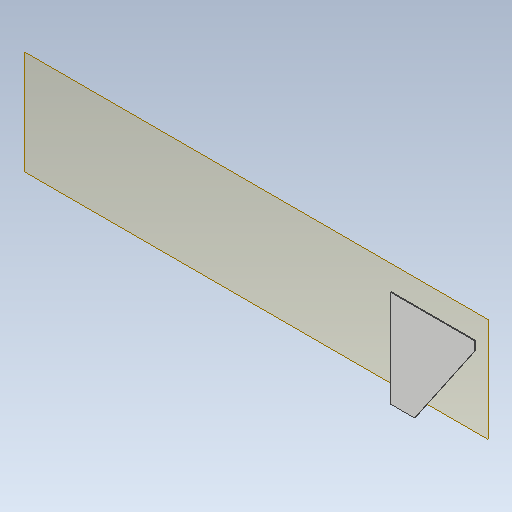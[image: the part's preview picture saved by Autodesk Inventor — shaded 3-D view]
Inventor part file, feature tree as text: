
AUTODESK INVENTOR PART (.ipt)
format: ipt  version: 2020.1 (Build 241239000, 239)  size: 121,344 bytes
history: native  units: mm
features: other x5, plane x1, sheet_metal_op x1, sketch x1
ambient origin geometry x8: Origin, YZ Plane, XZ Plane, XY Plane, X Axis, Y Axis, Z Axis, Center Point
bodies: Solid1 (feature_tree)
feature tree (8):
  plane  "Work Plane1"
  sheet_metal_op  "Face1"
  sketch  "Sketch1"  dims[d0=9.721484mm d1=2.0mm d2=200.0mm d3=20.0mm d4=230.0mm]
  other  "Plate1"
  other  "Definition1"
  parser-record x1  (decoder bookkeeping rows leaked as tree rows — omitted from the tree; the rows remain in map.json)
  other  "svejselære.iam"
  other  "plade:1"
note: 1 file-system path scrubbed to <path> (originals preserved in map.json)
